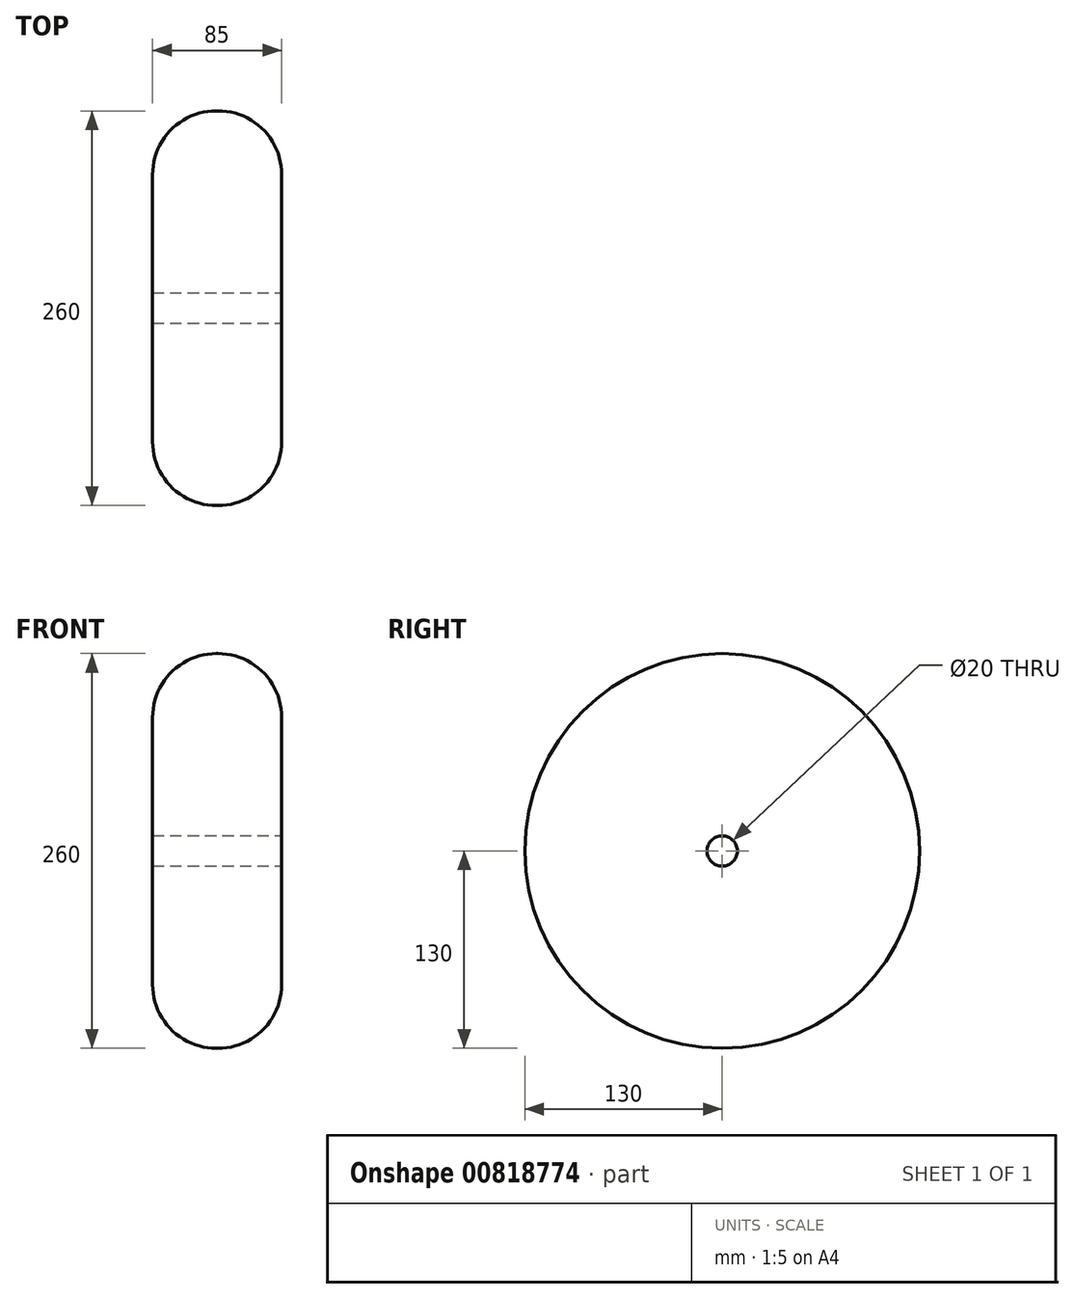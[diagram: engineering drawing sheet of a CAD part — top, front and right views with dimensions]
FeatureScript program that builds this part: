
annotation { "Feature Type Name" : "Feature", "Feature Type Description" : "" }
export const myFeature = defineFeature(function(context is Context, id is Id, definition is map)
    precondition{}
    {
        {
            var Q0;
            Q0=qCreatedBy(makeId("Right.planeOp"),FACE);
            var sketch = newSketch(context, id + "F0", { "sketchPlane" : qUnion([Q0])});
            skCircle(sketch, "E0", {"center": v(0, 0) * mm, "radius": 130 * mm});
            skSolve(sketch);
        }
        {
            var Q0;
            Q0=makeQuery(id+"F0.imprint","IMPRINT",FACE,{"disambiguationData":[TD([[makeQuery(id+"F0.imprint","IMPRINT",EDGE,{"derivedFrom":sQuery(id+"F0.wireOp",EDGE,"E0")}),1.0]])]});
            extrude(context, id + "F1", {"entities" : qUnion([Q0]), "depth" : 85 * mm, "offsetDistance" : 25 * mm});
        }
        {
            var Q0;
            Q0=makeQuery(id+"F1.opExtrude","CAP_FACE",FACE,{"disambiguationData":[OSD([sQuery(id+"F0.wireOp",EDGE,"E0")])],"isStart":false});
            var sketch = newSketch(context, id + "F2", { "sketchPlane" : qUnion([Q0])});
            skCircle(sketch, "E1", {"center": v(0, 0) * mm, "radius": 10 * mm});
            skSolve(sketch);
        }
        {
            var Q0;
            Q0=sQuery(id+"F2.wireOp",VERTEX,"E1.center");
            var Q1;
            Q1=makeQuery(id+"F1.opExtrude","SWEPT_BODY",BODY,{"disambiguationData":[OSD([sQuery(id+"F0.wireOp",EDGE,"E0")])]});
            hole(context, id + "F3", {"style" : HoleStyle.SIMPLE, "endStyle" : HoleEndStyle.BLIND, "holeDiameter" : 20 * mm, "majorDiameter" : 5 * mm, "holeDepth" : 85 * mm, "isTappedThrough" : true, "tappedDepth" : 12 * mm, "tapClearance" : 3, "locations" : qUnion([Q0]), "scope" : qUnion([Q1])});
        }
        {
            var Q0;
            Q0=makeQuery(id+"F1.opExtrude","CAP_EDGE",EDGE,{"disambiguationData":[OSD([sQuery(id+"F0.wireOp",EDGE,"E0")])],"isStart":true});
            var Q1;
            Q1=makeQuery(id+"F1.opExtrude","CAP_EDGE",EDGE,{"disambiguationData":[OSD([sQuery(id+"F0.wireOp",EDGE,"E0")])],"isStart":false});
            fillet(context, id + "F4", {"entities" : qUnion([Q0, Q1]), "radius" : 42 * mm, "tangentPropagation" : true, "allowEdgeOverflow" : false});
        }
    });
